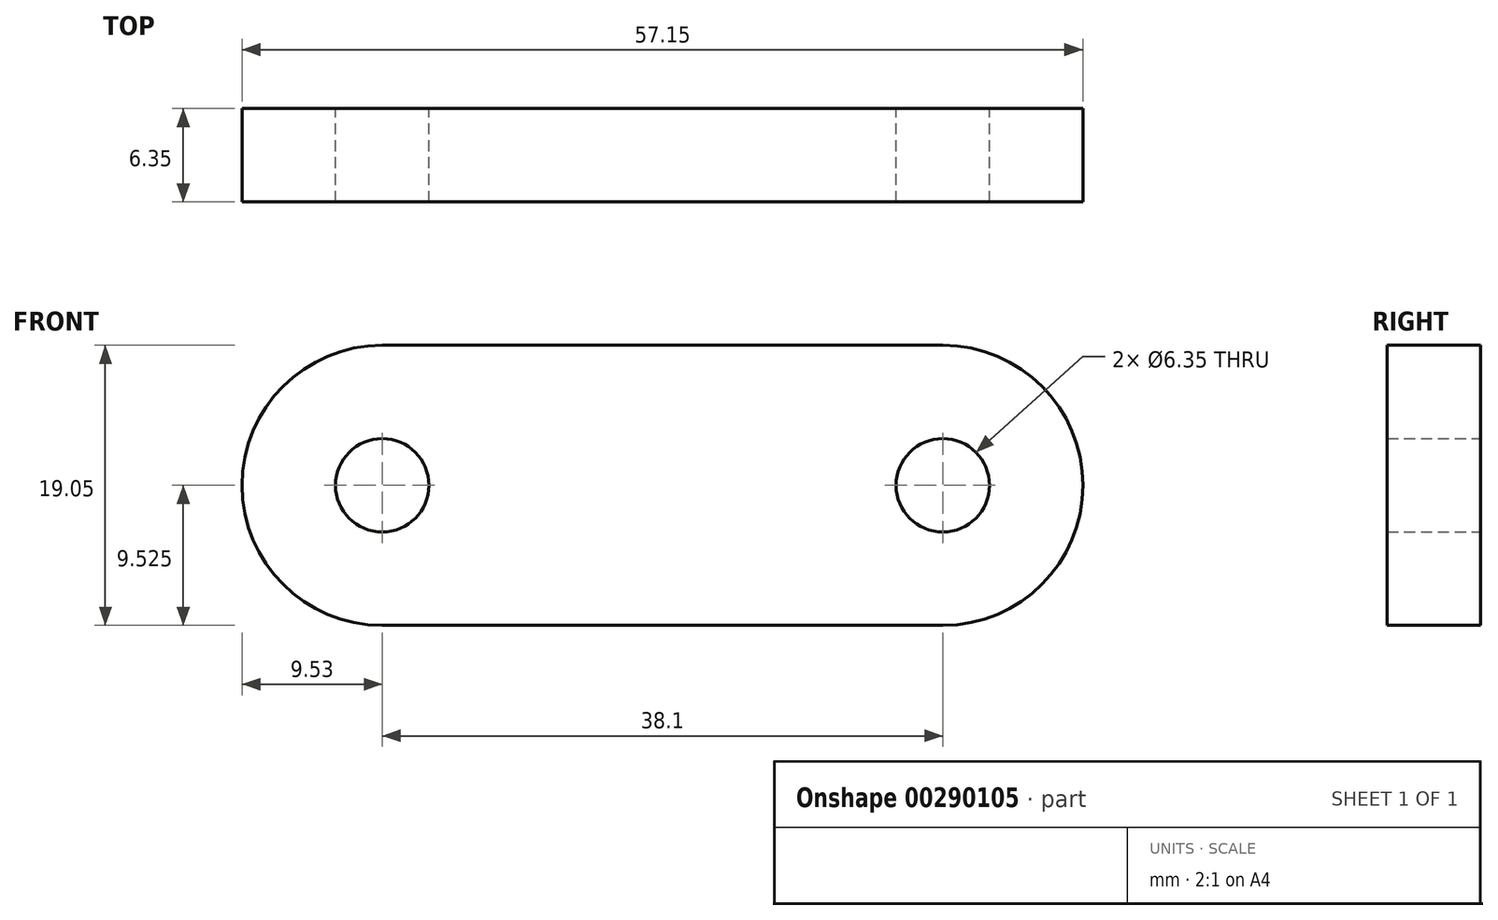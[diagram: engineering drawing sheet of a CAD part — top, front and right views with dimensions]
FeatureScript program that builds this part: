
annotation { "Feature Type Name" : "Feature", "Feature Type Description" : "" }
export const myFeature = defineFeature(function(context is Context, id is Id, definition is map)
    precondition{}
    {
        {
            var Q0;
            Q0=qCreatedBy(makeId("Front.planeOp"),FACE);
            var sketch = newSketch(context, id + "F0", { "sketchPlane" : qUnion([Q0])});
            skLineSegment(sketch, "E0.bottom", {"start": v(0, 0) * mm, "end": v(38.1, 0) * mm});
            skLineSegment(sketch, "E0.top", {"start": v(0, 19.05) * mm, "end": v(38.1, 19.05) * mm});
            skArc(sketch, "E1", {"start": v(0, 19.05) * mm, "mid": v(-9.53, 9.53) * mm, "end": v(0, 0) * mm});
            skArc(sketch, "E2", {"start": v(38.1, 0) * mm, "mid": v(47.62, 9.52) * mm, "end": v(38.1, 19.05) * mm});
            skCircle(sketch, "E3", {"center": v(0, 9.53) * mm, "radius": 3.18 * mm});
            skCircle(sketch, "E4", {"center": v(38.1, 9.53) * mm, "radius": 3.18 * mm});
            skSolve(sketch);
        }
        {
            var Q0;
            Q0 = qSketchRegion(id + "F0", true);
            extrude(context, id + "F1", {"entities" : qUnion([Q0]), "depth" : 6.35 * mm});
        }
    });
